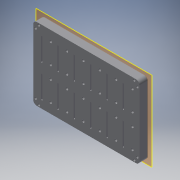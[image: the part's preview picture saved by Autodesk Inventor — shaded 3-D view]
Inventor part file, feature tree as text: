
AUTODESK INVENTOR PART (.ipt)
format: ipt  version: 2019.4 (Build 234330000, 330)  size: 265,728 bytes
history: native  units: mm
features: reference x8, other x5, extrude x3, sketch x3, plane x2, projected_geometry x2, pattern_linear x1
ambient origin geometry x8: Origin, YZ Plane, XZ Plane, XY Plane, X Axis, Y Axis, Z Axis, Center Point
bodies: Solid1 (feature_tree)
feature tree (24):
  plane  "Work Plane1"
  plane  "Work Plane2"
  extrude  "Extrusion1"  Depth=4.0mm TaperAngle=0.0deg
  extrude  "Extrusion2"  Depth=2.9mm
  extrude  "Extrusion3"  Depth=18.0mm
  pattern_linear  "Rectangular Pattern2"  Spacing1=0.2mm  [1 undecoded]
  sketch  "Sketch2"  dims[d0=9.3mm d1=0.0mm d3=4.0mm d4=0.0mm]
  reference  "Reference1"
  sketch  "Sketch3"  dims[d7=2.9mm d8=2.9mm]
  projected_geometry  "Projected Loop1"
  reference  "Reference2"
  reference  "Reference3"
  reference  "Reference4"
  reference  "Reference5"
  reference  "Reference6"
  sketch  "Sketch4"  dims[d19=1.0mm d20=0.0mm d21=60.0mm d23=18.0mm d24=20.0mm d26=36.0mm d35=0.2mm d36=0.2mm d37=0.2mm]
  reference  "Reference7"
  reference  "Reference8"
  projected_geometry  "Projected Loop3"
  other  "Full_HITscope_v0.iam"
  other  "05_Omniscope_base_v1:1"
  other  "Assembly_Omniscope_v1:11"
  other  "02_Camera_Lid:1"
  other  "00_electricpin_2.54_10x:2"
note: 1 required parameter value undecoded (feature->parameter linkage not recoverable at this tier; creation-order binding heuristic only, values carry confidence <= 0.55)
